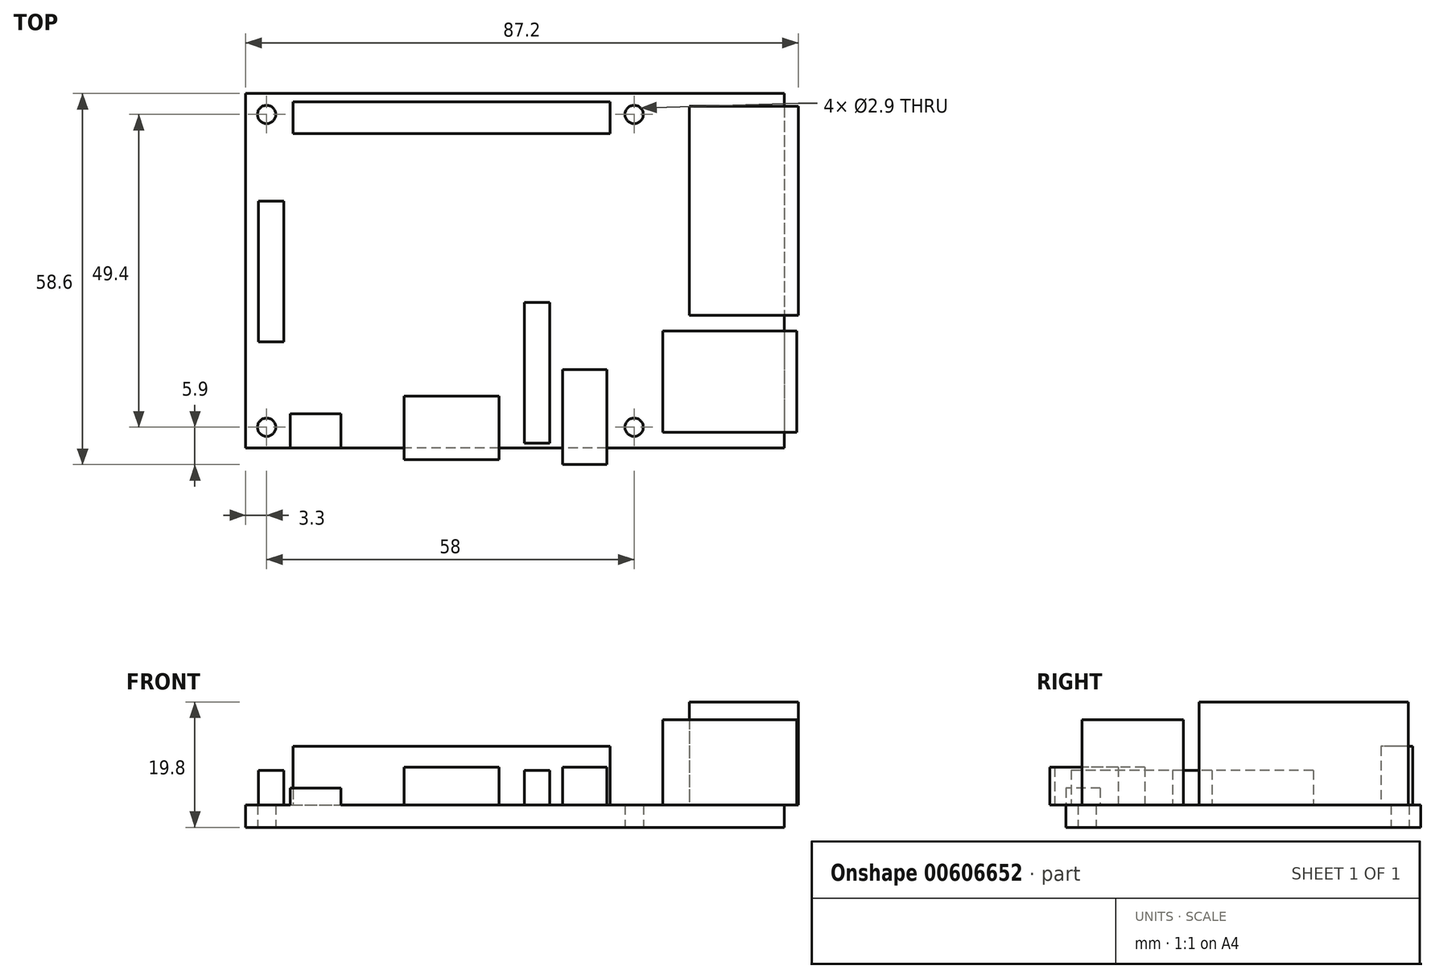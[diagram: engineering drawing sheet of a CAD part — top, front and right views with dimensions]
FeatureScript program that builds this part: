
annotation { "Feature Type Name" : "Feature", "Feature Type Description" : "" }
export const myFeature = defineFeature(function(context is Context, id is Id, definition is map)
    precondition{}
    {
        {
            var Q0;
            Q0=qCreatedBy(makeId("Top.planeOp"),FACE);
            var sketch = newSketch(context, id + "F0", { "sketchPlane" : qUnion([Q0])});
            skLineSegment(sketch, "E0.bottom", {"start": v(42.5, 28) * mm, "end": v(-42.5, 28) * mm});
            skLineSegment(sketch, "E0.top", {"start": v(42.5, -28) * mm, "end": v(-42.5, -28) * mm});
            skLineSegment(sketch, "E0.left", {"start": v(42.5, 28) * mm, "end": v(42.5, -28) * mm});
            skLineSegment(sketch, "E0.right", {"start": v(-42.5, 28) * mm, "end": v(-42.5, -28) * mm});
            skPoint(sketch, "E0.middle", {"position": v(0, 0) * mm});
            skPoint(sketch, "E1", {"position": v(-39.2, 24.7) * mm});
            skPoint(sketch, "E2", {"position": v(18.8, 24.7) * mm});
            skPoint(sketch, "E3", {"position": v(18.8, -24.7) * mm});
            skPoint(sketch, "E4", {"position": v(-39.2, -24.7) * mm});
            skSolve(sketch);
        }
        {
            var Q0;
            Q0=makeQuery(id+"F0.imprint","IMPRINT",FACE,{"disambiguationData":[TD([[makeQuery(id+"F0.imprint","IMPRINT",EDGE,{"derivedFrom":sQuery(id+"F0.wireOp",EDGE,"E0.bottom")}),1.0]])]});
            extrude(context, id + "F1", {"entities" : qUnion([Q0]), "depth" : 3.5 * mm, "offsetDistance" : 25 * mm});
        }
        {
            var Q0;
            Q0=makeQuery(id+"F1.opExtrude","CAP_FACE",FACE,{"disambiguationData":[OSD([sQuery(id+"F0.wireOp",EDGE,"E0.bottom"),sQuery(id+"F0.wireOp",EDGE,"E0.top"),sQuery(id+"F0.wireOp",EDGE,"E0.left"),sQuery(id+"F0.wireOp",EDGE,"E0.right")])],"isStart":false});
            var sketch = newSketch(context, id + "F2", { "sketchPlane" : qUnion([Q0])});
            skLineSegment(sketch, "E5.bottom", {"start": v(27.5, 26) * mm, "end": v(44.7, 26) * mm});
            skLineSegment(sketch, "E5.top", {"start": v(27.5, -7) * mm, "end": v(44.7, -7) * mm});
            skLineSegment(sketch, "E5.left", {"start": v(27.5, 26) * mm, "end": v(27.5, -7) * mm});
            skLineSegment(sketch, "E5.right", {"start": v(44.7, 26) * mm, "end": v(44.7, -7) * mm});
            skLineSegment(sketch, "E6.bottom", {"start": v(23.3, -9.5) * mm, "end": v(44.5, -9.5) * mm});
            skLineSegment(sketch, "E6.top", {"start": v(23.3, -25.5) * mm, "end": v(44.5, -25.5) * mm});
            skLineSegment(sketch, "E6.left", {"start": v(23.3, -9.5) * mm, "end": v(23.3, -25.5) * mm});
            skLineSegment(sketch, "E6.right", {"start": v(44.5, -9.5) * mm, "end": v(44.5, -25.5) * mm});
            skLineSegment(sketch, "E7.bottom", {"start": v(-35, 26.7) * mm, "end": v(15, 26.7) * mm});
            skLineSegment(sketch, "E7.top", {"start": v(-35, 21.7) * mm, "end": v(15, 21.7) * mm});
            skLineSegment(sketch, "E7.left", {"start": v(-35, 26.7) * mm, "end": v(-35, 21.7) * mm});
            skLineSegment(sketch, "E7.right", {"start": v(15, 26.7) * mm, "end": v(15, 21.7) * mm});
            skLineSegment(sketch, "E8.bottom", {"start": v(-40.5, 11) * mm, "end": v(-36.5, 11) * mm});
            skLineSegment(sketch, "E8.top", {"start": v(-40.5, -11.2) * mm, "end": v(-36.5, -11.2) * mm});
            skLineSegment(sketch, "E8.left", {"start": v(-40.5, 11) * mm, "end": v(-40.5, -11.2) * mm});
            skLineSegment(sketch, "E8.right", {"start": v(-36.5, 11) * mm, "end": v(-36.5, -11.2) * mm});
            skLineSegment(sketch, "E9.bottom", {"start": v(1.5, -5) * mm, "end": v(5.5, -5) * mm});
            skLineSegment(sketch, "E9.top", {"start": v(1.5, -27.2) * mm, "end": v(5.5, -27.2) * mm});
            skLineSegment(sketch, "E9.left", {"start": v(1.5, -5) * mm, "end": v(1.5, -27.2) * mm});
            skLineSegment(sketch, "E9.right", {"start": v(5.5, -5) * mm, "end": v(5.5, -27.2) * mm});
            skLineSegment(sketch, "E10.bottom", {"start": v(-35.5, -22.6) * mm, "end": v(-27.5, -22.6) * mm});
            skLineSegment(sketch, "E10.top", {"start": v(-35.5, -28) * mm, "end": v(-27.5, -28) * mm});
            skLineSegment(sketch, "E10.left", {"start": v(-35.5, -22.6) * mm, "end": v(-35.5, -28) * mm});
            skLineSegment(sketch, "E10.right", {"start": v(-27.5, -22.6) * mm, "end": v(-27.5, -28) * mm});
            skLineSegment(sketch, "E11.bottom", {"start": v(7.5, -15.6) * mm, "end": v(14.5, -15.6) * mm});
            skLineSegment(sketch, "E11.top", {"start": v(7.5, -30.6) * mm, "end": v(14.5, -30.6) * mm});
            skLineSegment(sketch, "E11.left", {"start": v(7.5, -15.6) * mm, "end": v(7.5, -30.6) * mm});
            skLineSegment(sketch, "E11.right", {"start": v(14.5, -15.6) * mm, "end": v(14.5, -30.6) * mm});
            skLineSegment(sketch, "E12.bottom", {"start": v(-17.5, -19.8) * mm, "end": v(-2.5, -19.8) * mm});
            skLineSegment(sketch, "E12.top", {"start": v(-17.5, -29.8) * mm, "end": v(-2.5, -29.8) * mm});
            skLineSegment(sketch, "E12.left", {"start": v(-17.5, -19.8) * mm, "end": v(-17.5, -29.8) * mm});
            skLineSegment(sketch, "E12.right", {"start": v(-2.5, -19.8) * mm, "end": v(-2.5, -29.8) * mm});
            skSolve(sketch);
        }
        {
            var Q0;
            Q0=makeQuery(id+"F2.imprint","IMPRINT",FACE,{"disambiguationData":[TD([[makeQuery(id+"F2.imprint","IMPRINT",EDGE,{"derivedFrom":sQuery(id+"F2.wireOp",EDGE,"E7.bottom")}),-1.0]])]});
            extrude(context, id + "F3", {"entities" : qUnion([Q0]), "operationType" : NewBodyOperationType.ADD, "depth" : 9.3 * mm, "offsetDistance" : 25 * mm});
        }
        {
            var Q0;
            Q0=makeQuery(id+"F2.imprint","IMPRINT",FACE,{"disambiguationData":[TD([[makeQuery(id+"F2.imprint","IMPRINT",EDGE,{"derivedFrom":sQuery(id+"F2.wireOp",EDGE,"E8.bottom")}),-1.0]])]});
            var Q1;
            Q1=makeQuery(id+"F2.imprint","IMPRINT",FACE,{"disambiguationData":[TD([[makeQuery(id+"F2.imprint","IMPRINT",EDGE,{"derivedFrom":sQuery(id+"F2.wireOp",EDGE,"E9.bottom")}),-1.0]])]});
            extrude(context, id + "F4", {"entities" : qUnion([Q0, Q1]), "operationType" : NewBodyOperationType.ADD, "depth" : 5.5 * mm, "offsetDistance" : 25 * mm});
        }
        {
            var Q0;
            Q0=makeQuery(id+"F2.imprint","IMPRINT",FACE,{"disambiguationData":[TD([[makeQuery(id+"F2.imprint","IMPRINT",EDGE,{"derivedFrom":sQuery(id+"F2.wireOp",EDGE,"E10.bottom")}),-1.0]])]});
            extrude(context, id + "F5", {"entities" : qUnion([Q0]), "operationType" : NewBodyOperationType.ADD, "depth" : 2.7 * mm, "offsetDistance" : 25 * mm});
        }
        {
            var Q0;
            {var subQ0=sQuery(id+"F2.wireOp",EDGE,"E12.top");Q0=makeQuery(id+"F2.imprint","IMPRINT",FACE,{"disambiguationData":[TD([[makeQuery(id+"F2.imprint","IMPRINT",EDGE,{"derivedFrom":subQ0}),1.0]])]});}
            var Q1;
            {var subQ0=sQuery(id+"F2.wireOp",EDGE,"E12.bottom");Q1=makeQuery(id+"F2.imprint","IMPRINT",FACE,{"disambiguationData":[TD([[makeQuery(id+"F2.imprint","IMPRINT",EDGE,{"derivedFrom":subQ0}),-1.0]])]});}
            extrude(context, id + "F6", {"entities" : qUnion([Q0, Q1]), "operationType" : NewBodyOperationType.ADD, "depth" : 6 * mm, "offsetDistance" : 25 * mm});
        }
        {
            var Q0;
            {var subQ0=sQuery(id+"F2.wireOp",EDGE,"E11.top");Q0=makeQuery(id+"F2.imprint","IMPRINT",FACE,{"disambiguationData":[TD([[makeQuery(id+"F2.imprint","IMPRINT",EDGE,{"derivedFrom":subQ0}),1.0]])]});}
            var Q1;
            {var subQ0=sQuery(id+"F2.wireOp",EDGE,"E11.bottom");Q1=makeQuery(id+"F2.imprint","IMPRINT",FACE,{"disambiguationData":[TD([[makeQuery(id+"F2.imprint","IMPRINT",EDGE,{"derivedFrom":subQ0}),-1.0]])]});}
            extrude(context, id + "F7", {"entities" : qUnion([Q0, Q1]), "operationType" : NewBodyOperationType.ADD, "depth" : 6 * mm, "offsetDistance" : 25 * mm});
        }
        {
            var Q0;
            {var subQ0=sQuery(id+"F2.wireOp",EDGE,"E5.left");Q0=makeQuery(id+"F2.imprint","IMPRINT",FACE,{"disambiguationData":[TD([[makeQuery(id+"F2.imprint","IMPRINT",EDGE,{"derivedFrom":subQ0}),1.0]])]});}
            var Q1;
            {var subQ0=sQuery(id+"F2.wireOp",EDGE,"E5.right");Q1=makeQuery(id+"F2.imprint","IMPRINT",FACE,{"disambiguationData":[TD([[makeQuery(id+"F2.imprint","IMPRINT",EDGE,{"derivedFrom":subQ0}),-1.0]])]});}
            extrude(context, id + "F8", {"entities" : qUnion([Q0, Q1]), "operationType" : NewBodyOperationType.ADD, "depth" : 16.3 * mm, "offsetDistance" : 25 * mm});
        }
        {
            var Q0;
            {var subQ0=sQuery(id+"F2.wireOp",EDGE,"E6.left");Q0=makeQuery(id+"F2.imprint","IMPRINT",FACE,{"disambiguationData":[TD([[makeQuery(id+"F2.imprint","IMPRINT",EDGE,{"derivedFrom":subQ0}),1.0]])]});}
            var Q1;
            {var subQ0=sQuery(id+"F2.wireOp",EDGE,"E6.right");Q1=makeQuery(id+"F2.imprint","IMPRINT",FACE,{"disambiguationData":[TD([[makeQuery(id+"F2.imprint","IMPRINT",EDGE,{"derivedFrom":subQ0}),-1.0]])]});}
            extrude(context, id + "F9", {"entities" : qUnion([Q0, Q1]), "operationType" : NewBodyOperationType.ADD, "depth" : 13.5 * mm, "offsetDistance" : 25 * mm});
        }
        {
            var Q0;
            Q0=sQuery(id+"F0.wireOp",VERTEX,"E2");
            var Q1;
            Q1=sQuery(id+"F0.wireOp",VERTEX,"E1");
            var Q2;
            Q2=sQuery(id+"F0.wireOp",VERTEX,"E4");
            var Q3;
            Q3=sQuery(id+"F0.wireOp",VERTEX,"E3");
            var Q4;
            Q4=makeQuery(id+"F1.opExtrude","SWEPT_BODY",BODY,{"disambiguationData":[OSD([sQuery(id+"F0.wireOp",EDGE,"E0.bottom"),sQuery(id+"F0.wireOp",EDGE,"E0.top"),sQuery(id+"F0.wireOp",EDGE,"E0.left"),sQuery(id+"F0.wireOp",EDGE,"E0.right")])]});
            hole(context, id + "F10", {"style" : HoleStyle.SIMPLE, "endStyle" : HoleEndStyle.THROUGH, "oppositeDirection" : true, "holeDiameter" : 2.9 * mm, "majorDiameter" : 5 * mm, "isTappedThrough" : true, "tappedDepth" : 3.5 * mm, "tapClearance" : 3, "locations" : qUnion([Q0, Q1, Q2, Q3]), "scope" : qUnion([Q4])});
        }
    });
